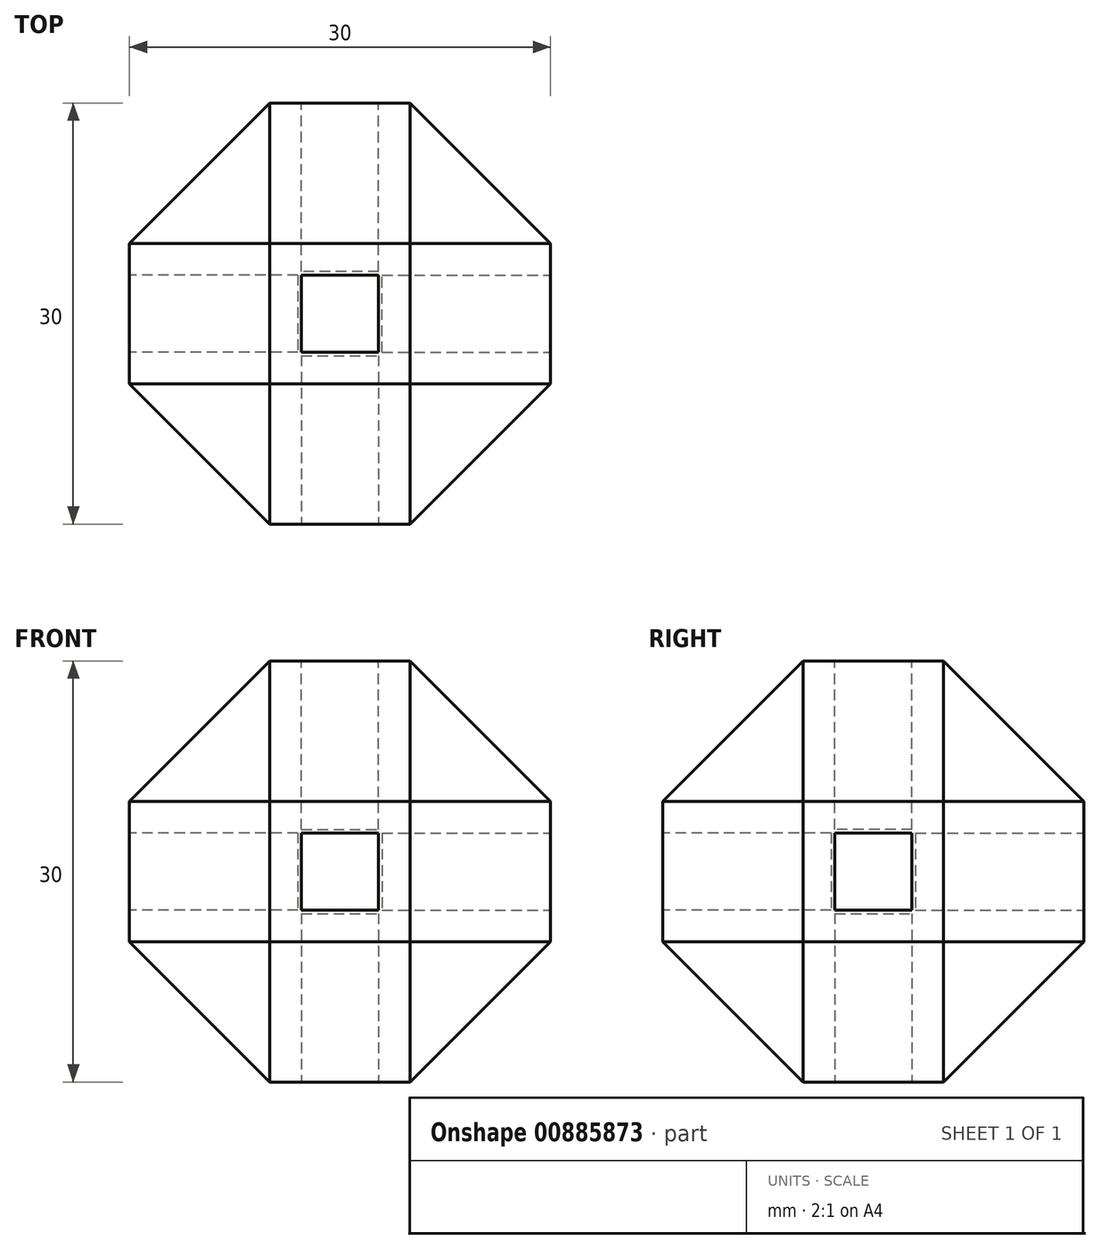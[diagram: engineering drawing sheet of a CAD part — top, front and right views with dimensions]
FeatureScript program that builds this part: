
annotation { "Feature Type Name" : "Feature", "Feature Type Description" : "" }
export const myFeature = defineFeature(function(context is Context, id is Id, definition is map)
    precondition{}
    {
        {
            var Q0;
            Q0=qCreatedBy(makeId("Top.planeOp"),FACE);
            var sketch = newSketch(context, id + "F0", { "sketchPlane" : qUnion([Q0])});
            skLineSegment(sketch, "E0.bottom", {"start": v(0, 0) * mm, "end": v(30, 0) * mm});
            skLineSegment(sketch, "E0.top", {"start": v(0, -30) * mm, "end": v(30, -30) * mm});
            skLineSegment(sketch, "E0.left", {"start": v(0, 0) * mm, "end": v(0, -30) * mm});
            skLineSegment(sketch, "E0.right", {"start": v(30, 0) * mm, "end": v(30, -30) * mm});
            skSolve(sketch);
        }
        {
            var Q0;
            Q0 = qSketchRegion(id + "F0", true);
            extrude(context, id + "F1", {"entities" : qUnion([Q0]), "depth" : 30 * mm, "offsetDistance" : 25 * mm});
        }
        {
            var Q0;
            Q0=makeQuery(id+"F1.opExtrude","SWEPT_FACE",FACE,{"disambiguationData":[OSD([sQuery(id+"F0.wireOp",EDGE,"E0.top")])]});
            var sketch = newSketch(context, id + "F2", { "sketchPlane" : qUnion([Q0])});
            skLineSegment(sketch, "E1.bottom", {"start": v(12.25, 17.75) * mm, "end": v(17.75, 17.75) * mm});
            skLineSegment(sketch, "E1.top", {"start": v(12.25, 12.25) * mm, "end": v(17.75, 12.25) * mm});
            skLineSegment(sketch, "E1.left", {"start": v(12.25, 17.75) * mm, "end": v(12.25, 12.25) * mm});
            skLineSegment(sketch, "E1.right", {"start": v(17.75, 17.75) * mm, "end": v(17.75, 12.25) * mm});
            skSolve(sketch);
        }
        {
            var Q0;
            Q0 = qSketchRegion(id + "F2", true);
            extrude(context, id + "F3", {"entities" : qUnion([Q0]), "operationType" : NewBodyOperationType.REMOVE, "oppositeDirection" : true, "depth" : 12 * mm, "offsetDistance" : 25 * mm});
        }
        {
            var Q0;
            Q0=makeQuery(id+"F1.opExtrude","SWEPT_FACE",FACE,{"disambiguationData":[OSD([sQuery(id+"F0.wireOp",EDGE,"E0.right")])]});
            var sketch = newSketch(context, id + "F4", { "sketchPlane" : qUnion([Q0])});
            skLineSegment(sketch, "E2.bottom", {"start": v(-17.75, 17.75) * mm, "end": v(-12.25, 17.75) * mm});
            skLineSegment(sketch, "E2.top", {"start": v(-17.75, 12.25) * mm, "end": v(-12.25, 12.25) * mm});
            skLineSegment(sketch, "E2.left", {"start": v(-17.75, 17.75) * mm, "end": v(-17.75, 12.25) * mm});
            skLineSegment(sketch, "E2.right", {"start": v(-12.25, 17.75) * mm, "end": v(-12.25, 12.25) * mm});
            skSolve(sketch);
        }
        {
            var Q0;
            Q0 = qSketchRegion(id + "F4", true);
            extrude(context, id + "F5", {"entities" : qUnion([Q0]), "operationType" : NewBodyOperationType.REMOVE, "oppositeDirection" : true, "depth" : 12 * mm, "offsetDistance" : 25 * mm});
        }
        {
            var Q0;
            Q0=makeQuery(id+"F1.opExtrude","SWEPT_FACE",FACE,{"disambiguationData":[OSD([sQuery(id+"F0.wireOp",EDGE,"E0.bottom")])]});
            var sketch = newSketch(context, id + "F6", { "sketchPlane" : qUnion([Q0])});
            skLineSegment(sketch, "E3.bottom", {"start": v(-17.75, 17.75) * mm, "end": v(-12.25, 17.75) * mm});
            skLineSegment(sketch, "E3.top", {"start": v(-17.75, 12.25) * mm, "end": v(-12.25, 12.25) * mm});
            skLineSegment(sketch, "E3.left", {"start": v(-17.75, 17.75) * mm, "end": v(-17.75, 12.25) * mm});
            skLineSegment(sketch, "E3.right", {"start": v(-12.25, 17.75) * mm, "end": v(-12.25, 12.25) * mm});
            skSolve(sketch);
        }
        {
            var Q0;
            Q0 = qSketchRegion(id + "F6", true);
            extrude(context, id + "F7", {"entities" : qUnion([Q0]), "operationType" : NewBodyOperationType.REMOVE, "oppositeDirection" : true, "depth" : 12 * mm, "offsetDistance" : 25 * mm});
        }
        {
            var Q0;
            Q0=makeQuery(id+"F1.opExtrude","SWEPT_FACE",FACE,{"disambiguationData":[OSD([sQuery(id+"F0.wireOp",EDGE,"E0.left")])]});
            var sketch = newSketch(context, id + "F8", { "sketchPlane" : qUnion([Q0])});
            skLineSegment(sketch, "E4.bottom", {"start": v(12.25, 17.75) * mm, "end": v(17.75, 17.75) * mm});
            skLineSegment(sketch, "E4.top", {"start": v(12.25, 12.25) * mm, "end": v(17.75, 12.25) * mm});
            skLineSegment(sketch, "E4.left", {"start": v(12.25, 17.75) * mm, "end": v(12.25, 12.25) * mm});
            skLineSegment(sketch, "E4.right", {"start": v(17.75, 17.75) * mm, "end": v(17.75, 12.25) * mm});
            skSolve(sketch);
        }
        {
            var Q0;
            Q0 = qSketchRegion(id + "F8", true);
            extrude(context, id + "F9", {"entities" : qUnion([Q0]), "operationType" : NewBodyOperationType.REMOVE, "oppositeDirection" : true, "depth" : 12 * mm, "offsetDistance" : 25 * mm});
        }
        {
            var Q0;
            Q0=makeQuery(id+"F1.opExtrude","CAP_FACE",FACE,{"disambiguationData":[OSD([sQuery(id+"F0.wireOp",EDGE,"E0.bottom"),sQuery(id+"F0.wireOp",EDGE,"E0.top"),sQuery(id+"F0.wireOp",EDGE,"E0.left"),sQuery(id+"F0.wireOp",EDGE,"E0.right")])],"isStart":false});
            var sketch = newSketch(context, id + "F10", { "sketchPlane" : qUnion([Q0])});
            skLineSegment(sketch, "E5.bottom", {"start": v(12.25, -12.25) * mm, "end": v(17.75, -12.25) * mm});
            skLineSegment(sketch, "E5.top", {"start": v(12.25, -17.75) * mm, "end": v(17.75, -17.75) * mm});
            skLineSegment(sketch, "E5.left", {"start": v(12.25, -12.25) * mm, "end": v(12.25, -17.75) * mm});
            skLineSegment(sketch, "E5.right", {"start": v(17.75, -12.25) * mm, "end": v(17.75, -17.75) * mm});
            skSolve(sketch);
        }
        {
            var Q0;
            Q0 = qSketchRegion(id + "F10", true);
            extrude(context, id + "F11", {"entities" : qUnion([Q0]), "operationType" : NewBodyOperationType.REMOVE, "oppositeDirection" : true, "depth" : 12 * mm, "offsetDistance" : 25 * mm});
        }
        {
            var Q0;
            Q0=makeQuery(id+"F1.opExtrude","CAP_FACE",FACE,{"disambiguationData":[OSD([sQuery(id+"F0.wireOp",EDGE,"E0.bottom"),sQuery(id+"F0.wireOp",EDGE,"E0.top"),sQuery(id+"F0.wireOp",EDGE,"E0.left"),sQuery(id+"F0.wireOp",EDGE,"E0.right")])],"isStart":true});
            var sketch = newSketch(context, id + "F12", { "sketchPlane" : qUnion([Q0])});
            skLineSegment(sketch, "E6.bottom", {"start": v(12.25, 17.75) * mm, "end": v(17.75, 17.75) * mm});
            skLineSegment(sketch, "E6.top", {"start": v(12.25, 12.25) * mm, "end": v(17.75, 12.25) * mm});
            skLineSegment(sketch, "E6.left", {"start": v(12.25, 17.75) * mm, "end": v(12.25, 12.25) * mm});
            skLineSegment(sketch, "E6.right", {"start": v(17.75, 17.75) * mm, "end": v(17.75, 12.25) * mm});
            skSolve(sketch);
        }
        {
            var Q0;
            Q0 = qSketchRegion(id + "F12", true);
            extrude(context, id + "F13", {"entities" : qUnion([Q0]), "operationType" : NewBodyOperationType.REMOVE, "oppositeDirection" : true, "depth" : 12 * mm, "offsetDistance" : 25 * mm});
        }
        {
            var Q0;
            Q0=makeQuery(id+"F1.opExtrude","CAP_EDGE",EDGE,{"disambiguationData":[OSD([sQuery(id+"F0.wireOp",EDGE,"E0.top")])],"isStart":true});
            var Q1;
            Q1=makeQuery(id+"F1.opExtrude","SWEPT_EDGE",EDGE,{"disambiguationData":[OSD([sQuery(id+"F0.wireOp",EDGE,"E0.top"),sQuery(id+"F0.wireOp",EDGE,"E0.right")])]});
            var Q2;
            Q2=makeQuery(id+"F1.opExtrude","CAP_EDGE",EDGE,{"disambiguationData":[OSD([sQuery(id+"F0.wireOp",EDGE,"E0.top")])],"isStart":false});
            var Q3;
            Q3=makeQuery(id+"F1.opExtrude","SWEPT_EDGE",EDGE,{"disambiguationData":[OSD([sQuery(id+"F0.wireOp",EDGE,"E0.top"),sQuery(id+"F0.wireOp",EDGE,"E0.left")])]});
            var Q4;
            Q4=makeQuery(id+"F1.opExtrude","CAP_EDGE",EDGE,{"disambiguationData":[OSD([sQuery(id+"F0.wireOp",EDGE,"E0.right")])],"isStart":true});
            var Q5;
            Q5=makeQuery(id+"F1.opExtrude","CAP_EDGE",EDGE,{"disambiguationData":[OSD([sQuery(id+"F0.wireOp",EDGE,"E0.left")])],"isStart":true});
            var Q6;
            Q6=makeQuery(id+"F1.opExtrude","CAP_EDGE",EDGE,{"disambiguationData":[OSD([sQuery(id+"F0.wireOp",EDGE,"E0.bottom")])],"isStart":true});
            var Q7;
            Q7=makeQuery(id+"F1.opExtrude","SWEPT_EDGE",EDGE,{"disambiguationData":[OSD([sQuery(id+"F0.wireOp",EDGE,"E0.bottom"),sQuery(id+"F0.wireOp",EDGE,"E0.right")])]});
            var Q8;
            Q8=makeQuery(id+"F1.opExtrude","CAP_EDGE",EDGE,{"disambiguationData":[OSD([sQuery(id+"F0.wireOp",EDGE,"E0.right")])],"isStart":false});
            var Q9;
            Q9=makeQuery(id+"F1.opExtrude","CAP_EDGE",EDGE,{"disambiguationData":[OSD([sQuery(id+"F0.wireOp",EDGE,"E0.left")])],"isStart":false});
            var Q10;
            Q10=makeQuery(id+"F1.opExtrude","CAP_EDGE",EDGE,{"disambiguationData":[OSD([sQuery(id+"F0.wireOp",EDGE,"E0.bottom")])],"isStart":false});
            var Q11;
            Q11=makeQuery(id+"F1.opExtrude","SWEPT_EDGE",EDGE,{"disambiguationData":[OSD([sQuery(id+"F0.wireOp",EDGE,"E0.bottom"),sQuery(id+"F0.wireOp",EDGE,"E0.left")])]});
            chamfer(context, id + "F14", {"entities" : qUnion([Q0, Q1, Q2, Q3, Q4, Q5, Q6, Q7, Q8, Q9, Q10, Q11]), "width" : 10 * mm, "tangentPropagation" : true});
        }
    });
